# Revit family: Andreu World_Smile_BQ0337
name_source: partatom
category: Mobiliario
revit_build: Autodesk Revit 2014 (Build: 20130722_2115(x64)
units: mm (PartAtom-declared; Revit-internal decimal feet)

## types (1)
- BQ-0337
    Depth = 470 mm  [stored 1.54199 ft]
    Descripción = Barstool with oak board seat and backrest and solid beech wood frame
    Fabricante = Andreu World
    Height = 1005 mm  [stored 3.29724 ft]
    Metal = Andreu World Polished Chrome Finish
    Modelo = Smile
    Reference = BQ-0337
    Seat = Andreu World Oak Vertical
    Seat Height = 770 mm  [stored 2.52625 ft]
    Structure Finish = Andreu World Beech V
    Structure Finish H = Andreu World Beech H
    URL = http://www.andreuworld.com
    Width = 470 mm  [stored 1.54199 ft]

note: [stored X ft] marks values corroborated as IEEE doubles in the binary element streams (Revit-internal decimal feet)

## geometry (parser evidence)
native form markers: Blend x10
no freeform markers — native parametric forms only
